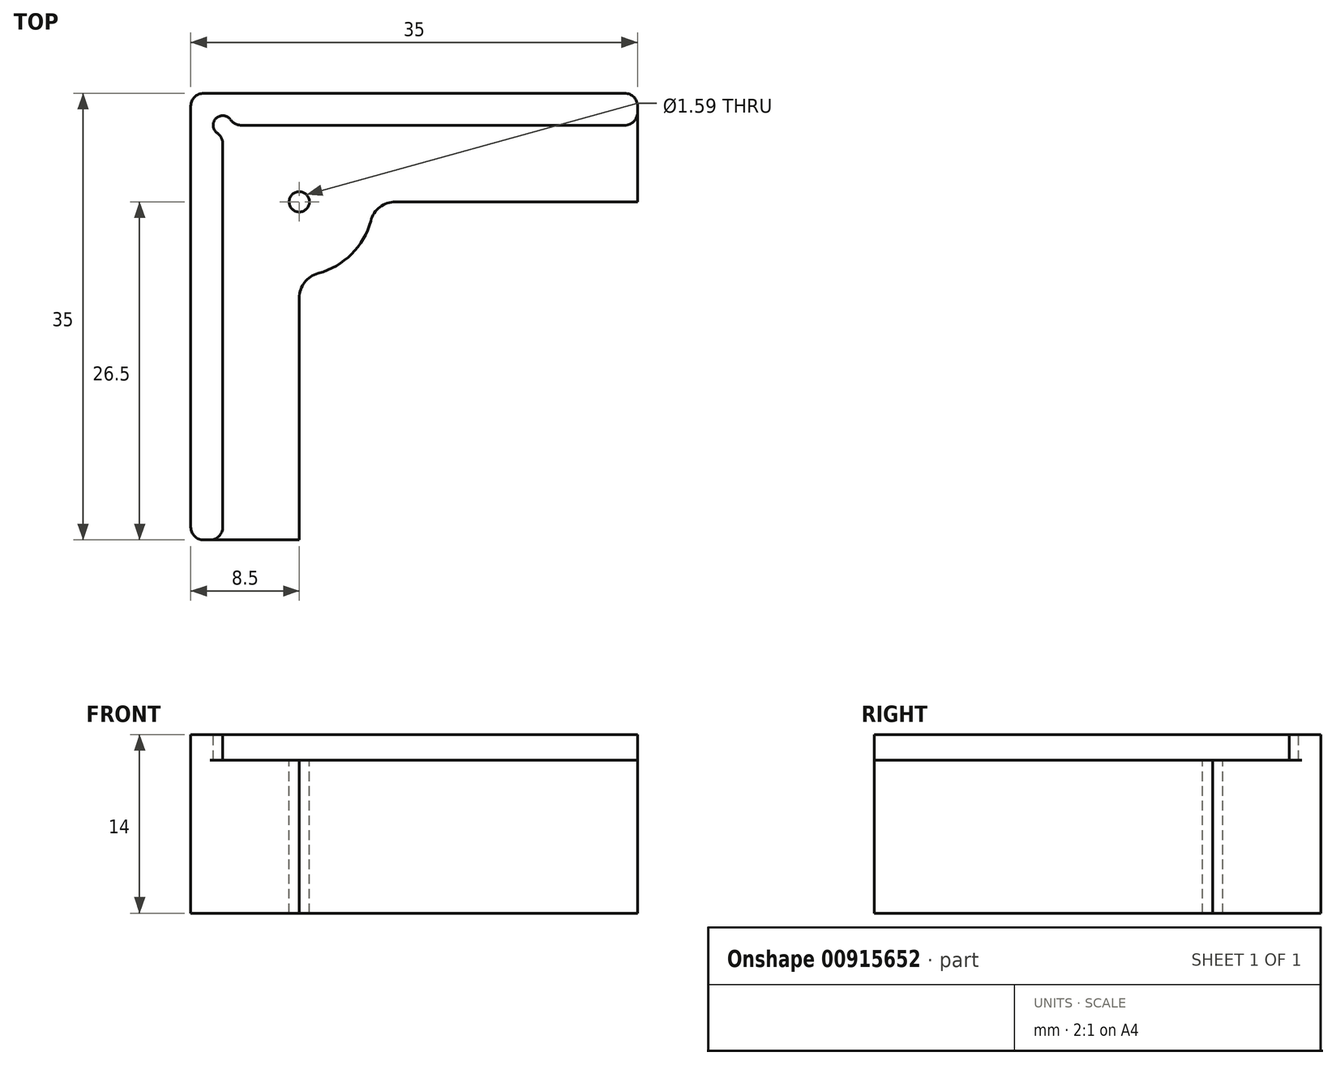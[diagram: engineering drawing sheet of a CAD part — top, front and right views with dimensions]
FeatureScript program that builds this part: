
annotation { "Feature Type Name" : "Feature", "Feature Type Description" : "" }
export const myFeature = defineFeature(function(context is Context, id is Id, definition is map)
    precondition{}
    {
        {
            var Q0;
            Q0=qCreatedBy(makeId("Top.planeOp"),FACE);
            var sketch = newSketch(context, id + "F0", { "sketchPlane" : qUnion([Q0])});
            skLineSegment(sketch, "E0.bottom", {"start": v(-17.5, 17.5) * mm, "end": v(17.5, 17.5) * mm});
            skLineSegment(sketch, "E0.top", {"start": v(-17.5, -17.5) * mm, "end": v(17.5, -17.5) * mm});
            skLineSegment(sketch, "E0.left", {"start": v(-17.5, 17.5) * mm, "end": v(-17.5, -17.5) * mm});
            skLineSegment(sketch, "E0.right", {"start": v(17.5, 17.5) * mm, "end": v(17.5, -17.5) * mm});
            skPoint(sketch, "E0.middle", {"position": v(0, 0) * mm});
            skSolve(sketch);
        }
        {
            var Q0;
            Q0 = qSketchRegion(id + "F0", true);
            extrude(context, id + "F1", {"entities" : qUnion([Q0]), "depth" : 12 * mm, "offsetDistance" : 25.4 * mm});
        }
        {
            var Q0;
            Q0=makeQuery(id+"F1.opExtrude","CAP_FACE",FACE,{"disambiguationData":[OSD([sQuery(id+"F0.wireOp",EDGE,"E0.bottom"),sQuery(id+"F0.wireOp",EDGE,"E0.top"),sQuery(id+"F0.wireOp",EDGE,"E0.left"),sQuery(id+"F0.wireOp",EDGE,"E0.right")])],"isStart":false});
            var sketch = newSketch(context, id + "F2", { "sketchPlane" : qUnion([Q0])});
            skLineSegment(sketch, "E1", {"start": v(-17.5, 17.5) * mm, "end": v(-17.5, -17.5) * mm});
            skLineSegment(sketch, "E2", {"start": v(-17.5, 17.5) * mm, "end": v(17.5, 17.5) * mm});
            skLineSegment(sketch, "E3", {"start": v(17.5, 15) * mm, "end": v(-15, 15) * mm});
            skLineSegment(sketch, "E4", {"start": v(-15, 15) * mm, "end": v(-15, -17.5) * mm});
            skLineSegment(sketch, "E5", {"start": v(-15, -17.5) * mm, "end": v(-17.5, -17.5) * mm});
            skLineSegment(sketch, "E6", {"start": v(17.5, 17.5) * mm, "end": v(17.5, 15) * mm});
            skSolve(sketch);
        }
        {
            var Q0;
            Q0 = qSketchRegion(id + "F2", true);
            extrude(context, id + "F3", {"entities" : qUnion([Q0]), "operationType" : NewBodyOperationType.ADD, "depth" : 2 * mm, "offsetDistance" : 25.4 * mm});
        }
        {
            var Q0;
            Q0=makeQuery(id+"F1.opExtrude","CAP_FACE",FACE,{"disambiguationData":[OSD([sQuery(id+"F0.wireOp",EDGE,"E0.bottom"),sQuery(id+"F0.wireOp",EDGE,"E0.top"),sQuery(id+"F0.wireOp",EDGE,"E0.left"),sQuery(id+"F0.wireOp",EDGE,"E0.right")])],"isStart":false});
            var sketch = newSketch(context, id + "F4", { "sketchPlane" : qUnion([Q0])});
            skCircle(sketch, "E7", {"center": v(-9, 9) * mm, "radius": 0.8 * mm});
            skSolve(sketch);
        }
        {
            var Q0;
            Q0 = qSketchRegion(id + "F4", true);
            extrude(context, id + "F5", {"entities" : qUnion([Q0]), "operationType" : NewBodyOperationType.REMOVE, "endBound" : BoundingType.THROUGH_ALL, "oppositeDirection" : true, "depth" : 25.4 * mm, "offsetDistance" : 25.4 * mm});
        }
        {
            var Q0;
            Q0=makeQuery(id+"F1.opExtrude","CAP_FACE",FACE,{"disambiguationData":[OSD([sQuery(id+"F0.wireOp",EDGE,"E0.bottom"),sQuery(id+"F0.wireOp",EDGE,"E0.top"),sQuery(id+"F0.wireOp",EDGE,"E0.left"),sQuery(id+"F0.wireOp",EDGE,"E0.right")])],"isStart":false});
            var sketch = newSketch(context, id + "F6", { "sketchPlane" : qUnion([Q0])});
            skArc(sketch, "E8", {"start": v(-3.2, 9) * mm, "mid": v(-4.9, 4.9) * mm, "end": v(-9, 3.2) * mm});
            skLineSegment(sketch, "E9", {"start": v(-9, 3.2) * mm, "end": v(-9, -12.5) * mm});
            skLineSegment(sketch, "E10", {"start": v(-9, -12.5) * mm, "end": v(12.5, -12.5) * mm});
            skLineSegment(sketch, "E11", {"start": v(12.5, -12.5) * mm, "end": v(12.5, 9) * mm});
            skLineSegment(sketch, "E12", {"start": v(12.5, 9) * mm, "end": v(-3.2, 9) * mm});
            skSolve(sketch);
        }
        {
            var Q0;
            Q0 = qSketchRegion(id + "F6", true);
            extrude(context, id + "F7", {"entities" : qUnion([Q0]), "operationType" : NewBodyOperationType.REMOVE, "endBound" : BoundingType.THROUGH_ALL, "oppositeDirection" : true, "depth" : 25.4 * mm, "offsetDistance" : 25.4 * mm});
        }
        {
            var Q0;
            Q0=makeQuery(id+"F3.opExtrude","CAP_FACE",FACE,{"disambiguationData":[OSD([sQuery(id+"F2.wireOp",EDGE,"E1"),sQuery(id+"F2.wireOp",EDGE,"E2"),sQuery(id+"F2.wireOp",EDGE,"E3"),sQuery(id+"F2.wireOp",EDGE,"E4"),sQuery(id+"F2.wireOp",EDGE,"E5"),sQuery(id+"F2.wireOp",EDGE,"E6")])],"isStart":false});
            var sketch = newSketch(context, id + "F8", { "sketchPlane" : qUnion([Q0])});
            skCircle(sketch, "E13", {"center": v(-15, 15) * mm, "radius": 0.75 * mm});
            skSolve(sketch);
        }
        {
            var Q0;
            Q0 = qSketchRegion(id + "F8", true);
            var Q1;
            Q1=makeQuery(id+"F1.opExtrude","CAP_FACE",FACE,{"disambiguationData":[OSD([sQuery(id+"F0.wireOp",EDGE,"E0.bottom"),sQuery(id+"F0.wireOp",EDGE,"E0.top"),sQuery(id+"F0.wireOp",EDGE,"E0.left"),sQuery(id+"F0.wireOp",EDGE,"E0.right")])],"isStart":false});
            extrude(context, id + "F9", {"entities" : qUnion([Q0]), "operationType" : NewBodyOperationType.REMOVE, "endBound" : BoundingType.UP_TO_SURFACE, "oppositeDirection" : true, "depth" : 25.4 * mm, "endBoundEntityFace" : qUnion([Q1]), "offsetDistance" : 25.4 * mm});
        }
        {
            var Q0;
            Q0=makeQuery(id+"F7.boolean.opBoolean","COPY",EDGE,{"derivedFrom":makeQuery(id+"F7.opExtrude","SWEPT_EDGE",EDGE,{"disambiguationData":[OSD([sQuery(id+"F6.wireOp",EDGE,"E8"),sQuery(id+"F6.wireOp",EDGE,"E12")])]})});
            var Q1;
            Q1=makeQuery(id+"F7.boolean.opBoolean","COPY",EDGE,{"derivedFrom":makeQuery(id+"F7.opExtrude","SWEPT_EDGE",EDGE,{"disambiguationData":[OSD([sQuery(id+"F6.wireOp",EDGE,"E8"),sQuery(id+"F6.wireOp",EDGE,"E9")])]})});
            var Q2;
            Q2=makeQuery(id+"F7.boolean.opBoolean","COPY",EDGE,{"derivedFrom":makeQuery(id+"F7.opExtrude","SWEPT_EDGE",EDGE,{"disambiguationData":[OSD([sQuery(id+"F6.wireOp",EDGE,"E11"),sQuery(id+"F6.wireOp",EDGE,"E12")])]})});
            var Q3;
            Q3=makeQuery(id+"F7.boolean.opBoolean","COPY",EDGE,{"derivedFrom":makeQuery(id+"F7.opExtrude","SWEPT_EDGE",EDGE,{"disambiguationData":[OSD([sQuery(id+"F6.wireOp",EDGE,"E10"),sQuery(id+"F6.wireOp",EDGE,"E11")])]})});
            var Q4;
            Q4=makeQuery(id+"F7.boolean.opBoolean","COPY",EDGE,{"derivedFrom":makeQuery(id+"F7.opExtrude","SWEPT_EDGE",EDGE,{"disambiguationData":[OSD([sQuery(id+"F6.wireOp",EDGE,"E9"),sQuery(id+"F6.wireOp",EDGE,"E10")])]})});
            fillet(context, id + "F10", {"entities" : qUnion([Q0, Q1, Q2, Q3, Q4]), "radius" : 2 * mm, "tangentPropagation" : true, "allowEdgeOverflow" : false});
        }
        {
            var Q0;
            Q0=makeQuery(id+"F9.boolean.opBoolean","MERGE",FACE,{"derivedFrom":[makeQuery(id+"F1.opExtrude","CAP_FACE",FACE,{"disambiguationData":[OSD([sQuery(id+"F0.wireOp",EDGE,"E0.bottom"),sQuery(id+"F0.wireOp",EDGE,"E0.top"),sQuery(id+"F0.wireOp",EDGE,"E0.left"),sQuery(id+"F0.wireOp",EDGE,"E0.right")])],"isStart":false})],"fromTools":[makeQuery(id+"F9.opExtrude","CAP_FACE",FACE,{"disambiguationData":[OSD([sQuery(id+"F8.wireOp",EDGE,"E13")])],"isStart":false})]});
            var sketch = newSketch(context, id + "F11", { "sketchPlane" : qUnion([Q0])});
            skLineSegment(sketch, "E14", {"start": v(-9, -10.5) * mm, "end": v(-9, -17.5) * mm});
            skLineSegment(sketch, "E15", {"start": v(10.5, 9) * mm, "end": v(17.5, 9) * mm});
            skLineSegment(sketch, "E16", {"start": v(17.5, 9) * mm, "end": v(17.5, -17.5) * mm});
            skLineSegment(sketch, "E17", {"start": v(17.5, -17.5) * mm, "end": v(-9, -17.5) * mm});
            skLineSegment(sketch, "E18", {"start": v(-9, -10.5) * mm, "end": v(10.5, 9) * mm});
            skSolve(sketch);
        }
        {
            var Q0;
            Q0 = qSketchRegion(id + "F11", true);
            extrude(context, id + "F12", {"entities" : qUnion([Q0]), "operationType" : NewBodyOperationType.REMOVE, "endBound" : BoundingType.THROUGH_ALL, "oppositeDirection" : true, "depth" : 25.4 * mm, "offsetDistance" : 25.4 * mm});
        }
        {
            var Q0;
            Q0=makeQuery(id+"F3.boolean.opBoolean","MERGE",EDGE,{"derivedFrom":[makeQuery(id+"F1.opExtrude","SWEPT_EDGE",EDGE,{"disambiguationData":[OSD([sQuery(id+"F0.wireOp",EDGE,"E0.bottom"),sQuery(id+"F0.wireOp",EDGE,"E0.right")])]}),makeQuery(id+"F3.opExtrude","SWEPT_EDGE",EDGE,{"disambiguationData":[OSD([sQuery(id+"F2.wireOp",EDGE,"E2"),sQuery(id+"F2.wireOp",EDGE,"E6")])]})]});
            var Q1;
            Q1=makeQuery(id+"F3.boolean.opBoolean","MERGE",EDGE,{"derivedFrom":[makeQuery(id+"F1.opExtrude","SWEPT_EDGE",EDGE,{"disambiguationData":[OSD([sQuery(id+"F0.wireOp",EDGE,"E0.top"),sQuery(id+"F0.wireOp",EDGE,"E0.left")])]}),makeQuery(id+"F3.opExtrude","SWEPT_EDGE",EDGE,{"disambiguationData":[OSD([sQuery(id+"F2.wireOp",EDGE,"E1"),sQuery(id+"F2.wireOp",EDGE,"E5")])]})]});
            var Q2;
            Q2=makeQuery(id+"F3.boolean.opBoolean","MERGE",EDGE,{"derivedFrom":[makeQuery(id+"F1.opExtrude","SWEPT_EDGE",EDGE,{"disambiguationData":[OSD([sQuery(id+"F0.wireOp",EDGE,"E0.bottom"),sQuery(id+"F0.wireOp",EDGE,"E0.left")])]}),makeQuery(id+"F3.opExtrude","SWEPT_EDGE",EDGE,{"disambiguationData":[OSD([sQuery(id+"F2.wireOp",EDGE,"E1"),sQuery(id+"F2.wireOp",EDGE,"E2")])]})]});
            var Q3;
            Q3=makeQuery(id+"F3.opExtrude","SWEPT_EDGE",EDGE,{"disambiguationData":[OSD([sQuery(id+"F0.wireOp",EDGE,"E0.top"),sQuery(id+"F2.wireOp",EDGE,"E4"),sQuery(id+"F2.wireOp",EDGE,"E5")])]});
            var Q4;
            Q4=makeQuery(id+"F3.opExtrude","SWEPT_EDGE",EDGE,{"disambiguationData":[OSD([sQuery(id+"F0.wireOp",EDGE,"E0.right"),sQuery(id+"F2.wireOp",EDGE,"E3"),sQuery(id+"F2.wireOp",EDGE,"E6")])]});
            var Q5;
            Q5=makeQuery(id+"F9.boolean.opBoolean","INTERSECT",EDGE,{"derivedFrom":[makeQuery(id+"F3.opExtrude","SWEPT_FACE",FACE,{"disambiguationData":[OSD([sQuery(id+"F2.wireOp",EDGE,"E4")])]}),makeQuery(id+"F9.opExtrude","SWEPT_FACE",FACE,{"disambiguationData":[OSD([sQuery(id+"F8.wireOp",EDGE,"E13")])]})]});
            var Q6;
            Q6=makeQuery(id+"F9.boolean.opBoolean","INTERSECT",EDGE,{"derivedFrom":[makeQuery(id+"F3.opExtrude","SWEPT_FACE",FACE,{"disambiguationData":[OSD([sQuery(id+"F2.wireOp",EDGE,"E3")])]}),makeQuery(id+"F9.opExtrude","SWEPT_FACE",FACE,{"disambiguationData":[OSD([sQuery(id+"F8.wireOp",EDGE,"E13")])]})]});
            var Q7;
            Q7=makeQuery(id+"F12.boolean.opBoolean","COPY",EDGE,{"derivedFrom":makeQuery(id+"F12.opExtrude","SWEPT_EDGE",EDGE,{"disambiguationData":[OSD([sQuery(id+"F0.wireOp",EDGE,"E0.top"),sQuery(id+"F11.wireOp",EDGE,"E14"),sQuery(id+"F11.wireOp",EDGE,"E17")])]})});
            var Q8;
            Q8=makeQuery(id+"F12.boolean.opBoolean","COPY",EDGE,{"derivedFrom":makeQuery(id+"F12.opExtrude","SWEPT_EDGE",EDGE,{"disambiguationData":[OSD([sQuery(id+"F0.wireOp",EDGE,"E0.right"),sQuery(id+"F11.wireOp",EDGE,"E15"),sQuery(id+"F11.wireOp",EDGE,"E16")])]})});
            fillet(context, id + "F13", {"entities" : qUnion([Q0, Q1, Q2, Q3, Q4, Q5, Q6, Q7, Q8]), "radius" : 1 * mm, "tangentPropagation" : true, "allowEdgeOverflow" : false});
        }
    });
